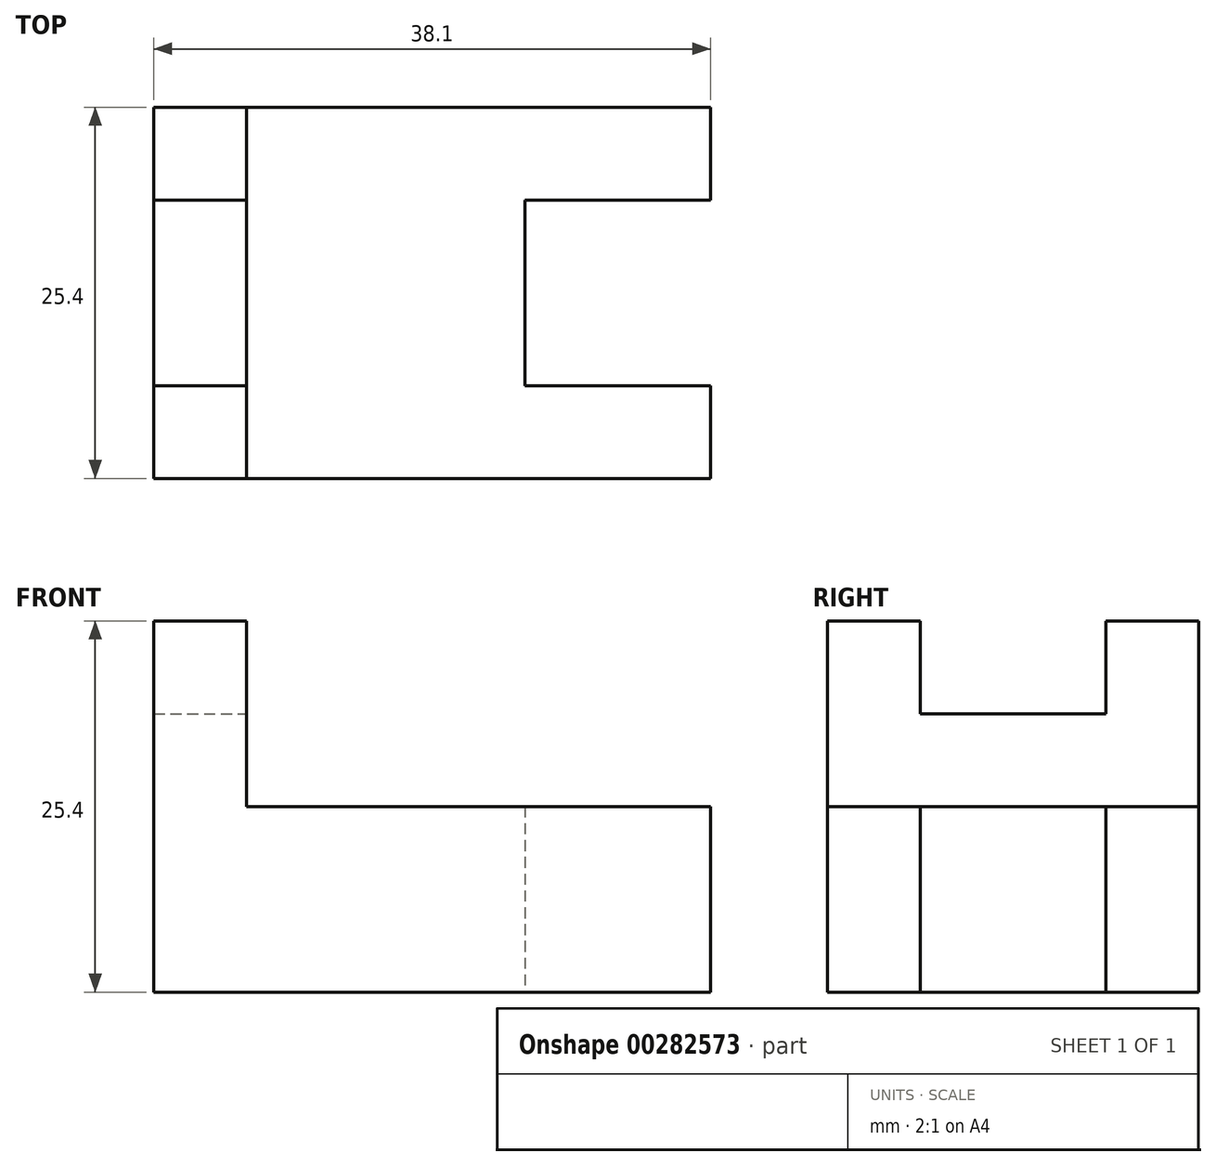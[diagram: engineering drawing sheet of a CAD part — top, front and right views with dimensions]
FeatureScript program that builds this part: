
annotation { "Feature Type Name" : "Feature", "Feature Type Description" : "" }
export const myFeature = defineFeature(function(context is Context, id is Id, definition is map)
    precondition{}
    {
        {
            var Q0;
            Q0=qCreatedBy(makeId("Top.planeOp"),FACE);
            var sketch = newSketch(context, id + "F0", { "sketchPlane" : qUnion([Q0])});
            skLineSegment(sketch, "E0", {"start": v(0, 0) * mm, "end": v(0, 25.4) * mm});
            skLineSegment(sketch, "E1", {"start": v(0, 25.4) * mm, "end": v(38.1, 25.4) * mm});
            skLineSegment(sketch, "E2", {"start": v(38.1, 25.4) * mm, "end": v(38.1, 0) * mm});
            skLineSegment(sketch, "E3", {"start": v(38.1, 0) * mm, "end": v(0, 0) * mm});
            skLineSegment(sketch, "E4", {"start": v(6.35, 25.4) * mm, "end": v(6.35, 0) * mm});
            skLineSegment(sketch, "E5", {"start": v(38.1, 19.05) * mm, "end": v(25.4, 19.05) * mm});
            skLineSegment(sketch, "E6", {"start": v(25.4, 19.05) * mm, "end": v(25.4, 6.35) * mm});
            skLineSegment(sketch, "E7", {"start": v(25.4, 6.35) * mm, "end": v(38.1, 6.35) * mm});
            skSolve(sketch);
        }
        {
            var Q0;
            {var subQ3=sQuery(id+"F0.wireOp",EDGE,"E4");Q0=makeQuery(id+"F0.imprint","IMPRINT",FACE,{"disambiguationData":[TD([[makeQuery(id+"F0.imprint","IMPRINT",EDGE,{"derivedFrom":subQ3}),1.0]])]});}
            extrude(context, id + "F1", {"entities" : qUnion([Q0]), "depth" : 12.7 * mm});
        }
        {
            var Q0;
            {var subQ0=sQuery(id+"F0.wireOp",EDGE,"E0");Q0=makeQuery(id+"F0.imprint","IMPRINT",FACE,{"disambiguationData":[TD([[makeQuery(id+"F0.imprint","IMPRINT",EDGE,{"derivedFrom":subQ0}),-1.0]])]});}
            extrude(context, id + "F2", {"entities" : qUnion([Q0]), "operationType" : NewBodyOperationType.ADD, "depth" : 25.4 * mm});
        }
        {
            var Q0;
            Q0=makeQuery(id+"F2.opExtrude","CAP_FACE",FACE,{"disambiguationData":[OSD([sQuery(id+"F0.wireOp",EDGE,"E0"),sQuery(id+"F0.wireOp",EDGE,"E1"),sQuery(id+"F0.wireOp",EDGE,"E3"),sQuery(id+"F0.wireOp",EDGE,"E4")])],"isStart":false});
            var sketch = newSketch(context, id + "F3", { "sketchPlane" : qUnion([Q0])});
            skLineSegment(sketch, "E8", {"start": v(0, 19.05) * mm, "end": v(6.35, 19.05) * mm});
            skLineSegment(sketch, "E9", {"start": v(0, 6.35) * mm, "end": v(6.35, 6.35) * mm});
            skSolve(sketch);
        }
        {
            var Q0;
            {var subQ0=sQuery(id+"F3.wireOp",EDGE,"E8");Q0=makeQuery(id+"F3.imprint","IMPRINT",FACE,{"disambiguationData":[TD([[makeQuery(id+"F3.imprint","IMPRINT",EDGE,{"derivedFrom":subQ0}),-1.0]])]});}
            extrude(context, id + "F4", {"entities" : qUnion([Q0]), "operationType" : NewBodyOperationType.REMOVE, "oppositeDirection" : true, "depth" : 6.35 * mm});
        }
    });
